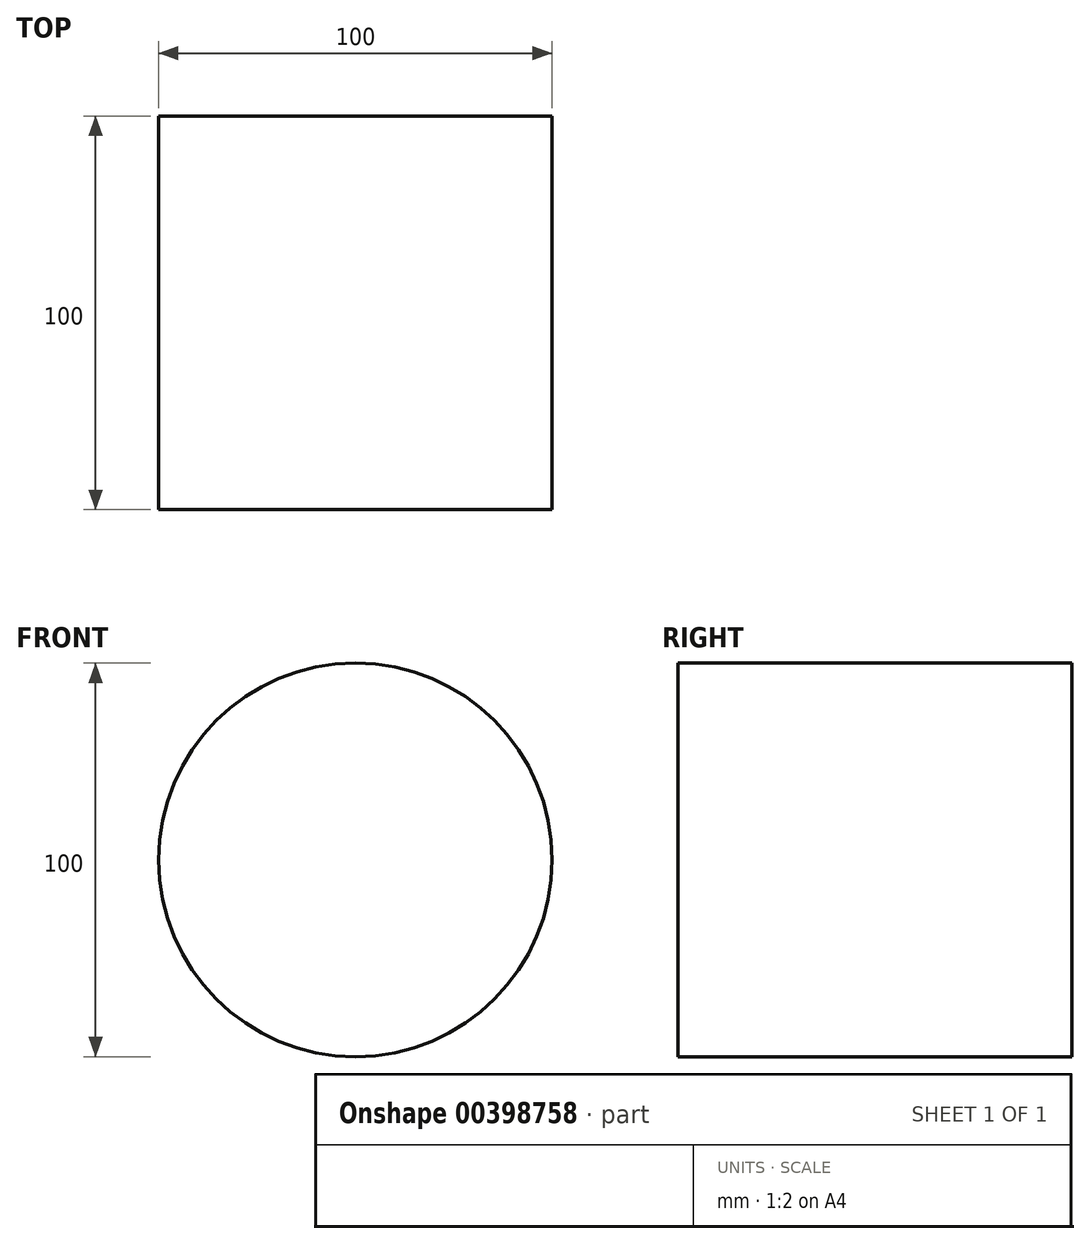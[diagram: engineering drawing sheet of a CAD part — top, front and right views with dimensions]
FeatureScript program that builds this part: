
annotation { "Feature Type Name" : "Feature", "Feature Type Description" : "" }
export const myFeature = defineFeature(function(context is Context, id is Id, definition is map)
    precondition{}
    {
        {
            var Q0;
            Q0=qCreatedBy(makeId("Front.planeOp"),FACE);
            var sketch = newSketch(context, id + "F0", { "sketchPlane" : qUnion([Q0])});
            skCircle(sketch, "E0", {"center": v(0, 0) * mm, "radius": 50 * mm});
            skSolve(sketch);
        }
        {
            var Q0;
            Q0 = qSketchRegion(id + "F0", true);
            extrude(context, id + "F1", {"entities" : qUnion([Q0]), "depth" : 100 * mm});
        }
    });
